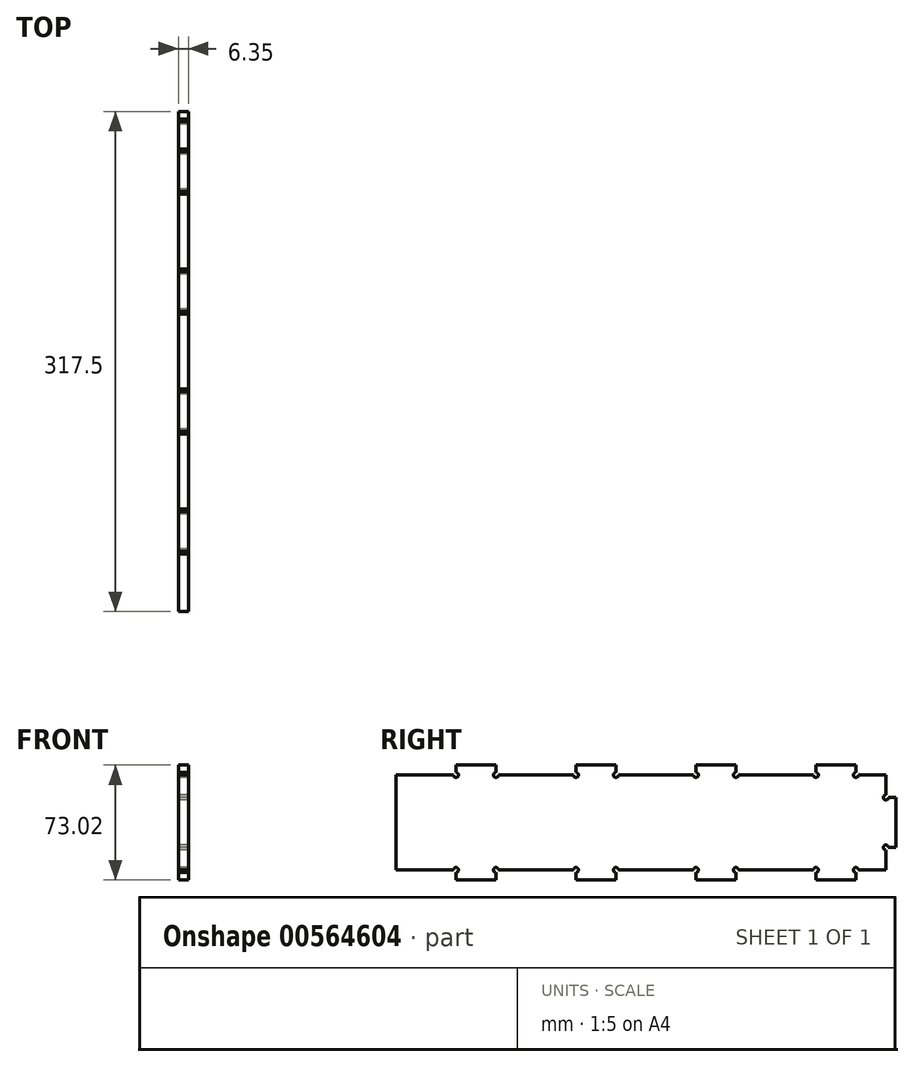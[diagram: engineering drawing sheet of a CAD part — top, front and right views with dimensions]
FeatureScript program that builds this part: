
annotation { "Feature Type Name" : "Feature", "Feature Type Description" : "" }
export const myFeature = defineFeature(function(context is Context, id is Id, definition is map)
    precondition{}
    {
        {
            var Q0;
            Q0=qCreatedBy(makeId("Right.planeOp"),FACE);
            var sketch = newSketch(context, id + "F0", { "sketchPlane" : qUnion([Q0])});
            skLineSegment(sketch, "E0.bottom", {"start": v(-139.7, 34.14) * mm, "end": v(171.45, 34.14) * mm});
            skLineSegment(sketch, "E0.top", {"start": v(-139.7, -26.18) * mm, "end": v(171.45, -26.18) * mm});
            skLineSegment(sketch, "E0.left", {"start": v(-139.7, 34.14) * mm, "end": v(-139.7, -26.18) * mm});
            skLineSegment(sketch, "E0.right", {"start": v(171.45, 34.14) * mm, "end": v(171.45, -26.18) * mm});
            skLineSegment(sketch, "E1.bottom", {"start": v(76.2, 34.14) * mm, "end": v(50.8, 34.14) * mm});
            skLineSegment(sketch, "E1.top", {"start": v(76.2, 40.5) * mm, "end": v(50.8, 40.5) * mm});
            skLineSegment(sketch, "E1.left", {"start": v(76.2, 34.14) * mm, "end": v(76.2, 40.5) * mm});
            skLineSegment(sketch, "E1.right", {"start": v(50.8, 34.14) * mm, "end": v(50.8, 40.5) * mm});
            skLineSegment(sketch, "E2.bottom", {"start": v(0, 34.14) * mm, "end": v(-25.4, 34.14) * mm});
            skLineSegment(sketch, "E2.top", {"start": v(0, 40.5) * mm, "end": v(-25.4, 40.5) * mm});
            skLineSegment(sketch, "E2.left", {"start": v(0, 34.14) * mm, "end": v(0, 40.5) * mm});
            skLineSegment(sketch, "E2.right", {"start": v(-25.4, 34.14) * mm, "end": v(-25.4, 40.5) * mm});
            skLineSegment(sketch, "E3.bottom", {"start": v(-76.2, 34.14) * mm, "end": v(-101.6, 34.14) * mm});
            skLineSegment(sketch, "E3.top", {"start": v(-76.2, 40.5) * mm, "end": v(-101.6, 40.5) * mm});
            skLineSegment(sketch, "E3.left", {"start": v(-76.2, 34.14) * mm, "end": v(-76.2, 40.5) * mm});
            skLineSegment(sketch, "E3.right", {"start": v(-101.6, 34.14) * mm, "end": v(-101.6, 40.5) * mm});
            skLineSegment(sketch, "E4.bottom", {"start": v(76.2, -26.18) * mm, "end": v(50.8, -26.18) * mm});
            skLineSegment(sketch, "E4.top", {"start": v(76.2, -32.53) * mm, "end": v(50.8, -32.53) * mm});
            skLineSegment(sketch, "E4.left", {"start": v(76.2, -26.18) * mm, "end": v(76.2, -32.53) * mm});
            skLineSegment(sketch, "E4.right", {"start": v(50.8, -26.18) * mm, "end": v(50.8, -32.53) * mm});
            skLineSegment(sketch, "E5.bottom", {"start": v(0, -26.18) * mm, "end": v(-25.4, -26.18) * mm});
            skLineSegment(sketch, "E5.top", {"start": v(0, -32.53) * mm, "end": v(-25.4, -32.53) * mm});
            skLineSegment(sketch, "E5.left", {"start": v(0, -26.18) * mm, "end": v(0, -32.53) * mm});
            skLineSegment(sketch, "E5.right", {"start": v(-25.4, -26.18) * mm, "end": v(-25.4, -32.53) * mm});
            skLineSegment(sketch, "E6.bottom", {"start": v(-76.2, -26.18) * mm, "end": v(-101.6, -26.18) * mm});
            skLineSegment(sketch, "E6.top", {"start": v(-76.2, -32.53) * mm, "end": v(-101.6, -32.53) * mm});
            skLineSegment(sketch, "E6.left", {"start": v(-76.2, -26.18) * mm, "end": v(-76.2, -32.53) * mm});
            skLineSegment(sketch, "E6.right", {"start": v(-101.6, -26.18) * mm, "end": v(-101.6, -32.53) * mm});
            skLineSegment(sketch, "E7.bottom", {"start": v(171.45, 19.86) * mm, "end": v(177.8, 19.86) * mm});
            skLineSegment(sketch, "E7.top", {"start": v(171.45, -11.9) * mm, "end": v(177.8, -11.9) * mm});
            skLineSegment(sketch, "E7.left", {"start": v(171.45, 19.86) * mm, "end": v(171.45, -11.9) * mm});
            skLineSegment(sketch, "E7.right", {"start": v(177.8, 19.86) * mm, "end": v(177.8, -11.9) * mm});
            skLineSegment(sketch, "E8.bottom", {"start": v(127, 34.14) * mm, "end": v(152.4, 34.14) * mm});
            skLineSegment(sketch, "E8.top", {"start": v(127, 40.5) * mm, "end": v(152.4, 40.5) * mm});
            skLineSegment(sketch, "E8.left", {"start": v(127, 34.14) * mm, "end": v(127, 40.5) * mm});
            skLineSegment(sketch, "E8.right", {"start": v(152.4, 34.14) * mm, "end": v(152.4, 40.5) * mm});
            skLineSegment(sketch, "E9.bottom", {"start": v(152.4, -26.18) * mm, "end": v(127, -26.18) * mm});
            skLineSegment(sketch, "E9.top", {"start": v(152.4, -32.53) * mm, "end": v(127, -32.53) * mm});
            skLineSegment(sketch, "E9.left", {"start": v(152.4, -26.18) * mm, "end": v(152.4, -32.53) * mm});
            skLineSegment(sketch, "E9.right", {"start": v(127, -26.18) * mm, "end": v(127, -32.53) * mm});
            skCircle(sketch, "E10", {"center": v(-101.6, 34.14) * mm, "radius": 1.59 * mm});
            skCircle(sketch, "E11", {"center": v(-76.2, 34.14) * mm, "radius": 1.59 * mm});
            skCircle(sketch, "E12", {"center": v(-25.4, 34.14) * mm, "radius": 1.59 * mm});
            skCircle(sketch, "E13", {"center": v(0, 34.14) * mm, "radius": 1.59 * mm});
            skCircle(sketch, "E14", {"center": v(50.8, 34.14) * mm, "radius": 1.59 * mm});
            skCircle(sketch, "E15", {"center": v(76.2, 34.14) * mm, "radius": 1.59 * mm});
            skCircle(sketch, "E16", {"center": v(127, 34.14) * mm, "radius": 1.59 * mm});
            skCircle(sketch, "E17", {"center": v(152.4, 34.14) * mm, "radius": 1.59 * mm});
            skCircle(sketch, "E18", {"center": v(127, -26.18) * mm, "radius": 1.59 * mm});
            skCircle(sketch, "E19", {"center": v(152.4, -26.18) * mm, "radius": 1.59 * mm});
            skCircle(sketch, "E20", {"center": v(76.2, -26.18) * mm, "radius": 1.59 * mm});
            skCircle(sketch, "E21", {"center": v(50.8, -26.18) * mm, "radius": 1.59 * mm});
            skCircle(sketch, "E22", {"center": v(0, -26.18) * mm, "radius": 1.59 * mm});
            skCircle(sketch, "E23", {"center": v(-25.4, -26.18) * mm, "radius": 1.59 * mm});
            skCircle(sketch, "E24", {"center": v(-76.2, -26.18) * mm, "radius": 1.59 * mm});
            skCircle(sketch, "E25", {"center": v(-101.6, -26.18) * mm, "radius": 1.59 * mm});
            skCircle(sketch, "E26", {"center": v(171.45, -11.9) * mm, "radius": 1.59 * mm});
            skCircle(sketch, "E27", {"center": v(171.45, 19.86) * mm, "radius": 1.59 * mm});
            skSolve(sketch);
        }
        {
            var Q0;
            {var subQ53=sQuery(id+"F0.wireOp",EDGE,"E0.left");Q0=makeQuery(id+"F0.imprint","IMPRINT",FACE,{"disambiguationData":[TD([[makeQuery(id+"F0.imprint","IMPRINT",EDGE,{"derivedFrom":subQ53}),1.0]])]});}
            var Q1;
            {var subQ1=sQuery(id+"F0.wireOp",EDGE,"E3.top");Q1=makeQuery(id+"F0.imprint","IMPRINT",FACE,{"disambiguationData":[TD([[makeQuery(id+"F0.imprint","IMPRINT",EDGE,{"derivedFrom":subQ1}),1.0]])]});}
            var Q2;
            {var subQ1=sQuery(id+"F0.wireOp",EDGE,"E2.top");Q2=makeQuery(id+"F0.imprint","IMPRINT",FACE,{"disambiguationData":[TD([[makeQuery(id+"F0.imprint","IMPRINT",EDGE,{"derivedFrom":subQ1}),1.0]])]});}
            var Q3;
            {var subQ1=sQuery(id+"F0.wireOp",EDGE,"E1.top");Q3=makeQuery(id+"F0.imprint","IMPRINT",FACE,{"disambiguationData":[TD([[makeQuery(id+"F0.imprint","IMPRINT",EDGE,{"derivedFrom":subQ1}),1.0]])]});}
            var Q4;
            {var subQ1=sQuery(id+"F0.wireOp",EDGE,"E8.top");Q4=makeQuery(id+"F0.imprint","IMPRINT",FACE,{"disambiguationData":[TD([[makeQuery(id+"F0.imprint","IMPRINT",EDGE,{"derivedFrom":subQ1}),-1.0]])]});}
            var Q5;
            {var subQ0=sQuery(id+"F0.wireOp",EDGE,"E7.right");Q5=makeQuery(id+"F0.imprint","IMPRINT",FACE,{"disambiguationData":[TD([[makeQuery(id+"F0.imprint","IMPRINT",EDGE,{"derivedFrom":subQ0}),-1.0]])]});}
            var Q6;
            {var subQ1=sQuery(id+"F0.wireOp",EDGE,"E9.top");Q6=makeQuery(id+"F0.imprint","IMPRINT",FACE,{"disambiguationData":[TD([[makeQuery(id+"F0.imprint","IMPRINT",EDGE,{"derivedFrom":subQ1}),-1.0]])]});}
            var Q7;
            {var subQ1=sQuery(id+"F0.wireOp",EDGE,"E4.top");Q7=makeQuery(id+"F0.imprint","IMPRINT",FACE,{"disambiguationData":[TD([[makeQuery(id+"F0.imprint","IMPRINT",EDGE,{"derivedFrom":subQ1}),-1.0]])]});}
            var Q8;
            {var subQ1=sQuery(id+"F0.wireOp",EDGE,"E5.top");Q8=makeQuery(id+"F0.imprint","IMPRINT",FACE,{"disambiguationData":[TD([[makeQuery(id+"F0.imprint","IMPRINT",EDGE,{"derivedFrom":subQ1}),-1.0]])]});}
            var Q9;
            {var subQ1=sQuery(id+"F0.wireOp",EDGE,"E6.top");Q9=makeQuery(id+"F0.imprint","IMPRINT",FACE,{"disambiguationData":[TD([[makeQuery(id+"F0.imprint","IMPRINT",EDGE,{"derivedFrom":subQ1}),-1.0]])]});}
            extrude(context, id + "F1", {"entities" : qUnion([Q0, Q1, Q2, Q3, Q4, Q5, Q6, Q7, Q8, Q9]), "depth" : 6.35 * mm, "offsetDistance" : 25.4 * mm});
        }
    });
